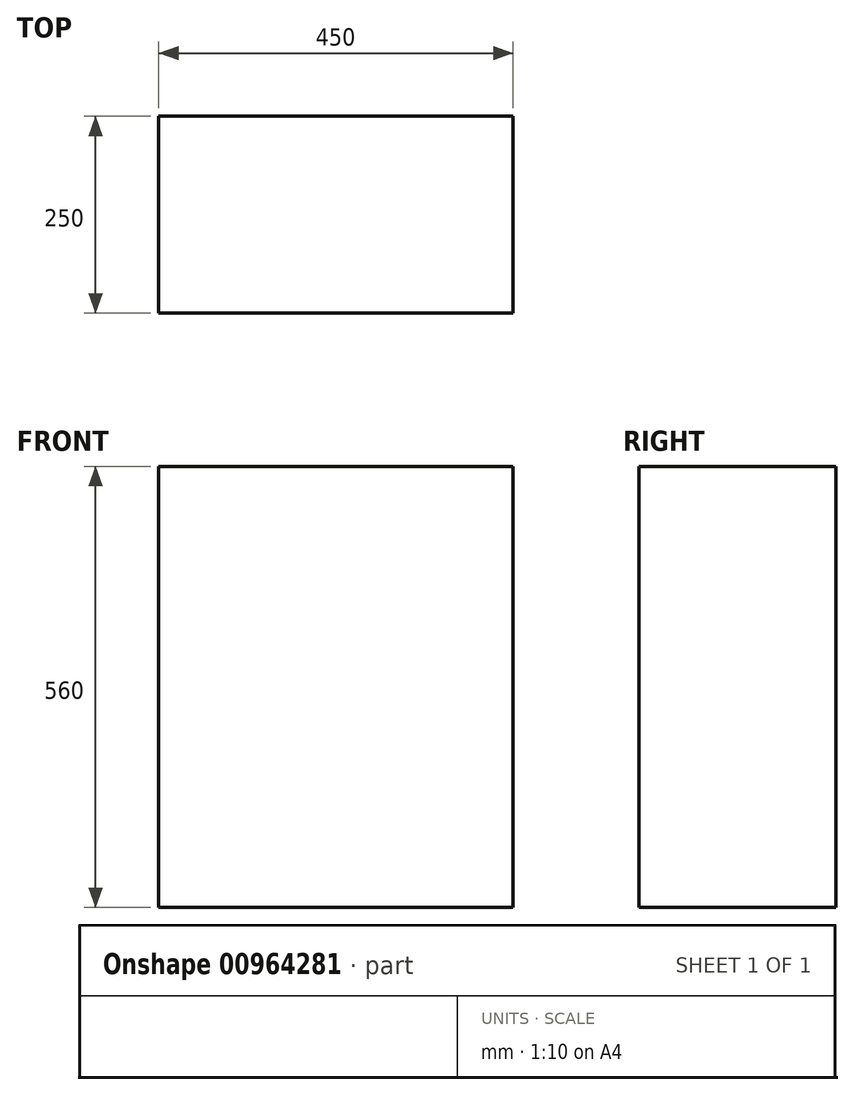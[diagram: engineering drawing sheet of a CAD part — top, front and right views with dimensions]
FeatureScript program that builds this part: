
annotation { "Feature Type Name" : "Feature", "Feature Type Description" : "" }
export const myFeature = defineFeature(function(context is Context, id is Id, definition is map)
    precondition{}
    {
        {
            var Q0;
            Q0=qCreatedBy(makeId("Front.planeOp"),FACE);
            var sketch = newSketch(context, id + "F0", { "sketchPlane" : qUnion([Q0])});
            skLineSegment(sketch, "E0.bottom", {"start": v(-225, 0) * mm, "end": v(225, 0) * mm});
            skLineSegment(sketch, "E0.top", {"start": v(-225, 560) * mm, "end": v(225, 560) * mm});
            skLineSegment(sketch, "E0.left", {"start": v(-225, 0) * mm, "end": v(-225, 560) * mm});
            skLineSegment(sketch, "E0.right", {"start": v(225, 0) * mm, "end": v(225, 560) * mm});
            skSolve(sketch);
        }
        {
            var Q0;
            Q0 = qSketchRegion(id + "F0", true);
            extrude(context, id + "F1", {"entities" : qUnion([Q0]), "depth" : 250 * mm, "offsetDistance" : 25 * mm});
        }
    });
